# Revit family: XLWH_SUPPLY
name_source: partatom
category: Mechanical Equipment
units: mm (PartAtom-declared; Revit-internal decimal feet)

## family parameters
Always vertical = Yes
Cut with Voids When Loaded = No
Part Type = Normal
Room Calculation Point = No
Round Connector Dimension = Use Diameter
Shared = No
Work Plane-Based = No

## types (8) — shared parameters
0 = 0' - 0"
1" = 0' - 1"
1.5 = 0' - 1 1/2"
1/2 = 0' - 0 1/2"
2" = 0' - 2"
2' = 2' - 0"
3" = 0' - 3"
4" = 0' - 4"
4'6" = 4' - 6"
9" = 0' - 9"
Manufacturer = Loren Cook Company
Model = XLWH_Supply
ONE EIGTH = 0' - 0 1/8"
Type Comments = Heavy Duty Low-Pressure Wall Supply Fan Steel Propeller Belt Drive
URL = www.lorencook.com

## per-type parameters (varying)
- 24_XLWH_SUPPLY: (A/2)-1"=1' - 2 27/32"; (A/2)-C-.5"=0' - 7 27/32"; (D_SUP/2)-(C/2)-.125"=0' - 11 1/2"; (SIZE/2)-.25"=1' - 2 11/16"; -((A/2)-C-.5")=-0' - 7 27/32"; -((SIZE/2)-.25")=-1' - 2 11/16"; -B=-1' - 7 1/16"; -B+1"=-1' - 5 1/16"; -C/2=-0' - 3 3/8"; -D=-0' - 3"; A=2' - 6 3/16"; A/2=1' - 3 3/32"; A/3.5=0' - 8 5/8"; A/7=0' - 4 5/16"; B=1' - 7 1/16"; B/2=0' - 9 17/32"; B/4=0' - 4 25/32"; C=0' - 6 3/4"; C/2=0' - 3 3/8"; D=2' - 6"; D/2=1' - 3"; E=0' - 3"; E/2=0' - 1 1/2"; MOTOR=0' - 3"; SIZE=2' - 5 7/8"; SIZE/2=1' - 2 15/16"
- 30_XLWH_SUPPLY: (A/2)-1"=1' - 5 27/32"; (A/2)-C-.5"=0' - 10 27/32"; (D_SUP/2)-(C/2)-.125"=1' - 2 1/2"; (SIZE/2)-.25"=1' - 5 11/16"; -((A/2)-C-.5")=-0' - 10 27/32"; -((SIZE/2)-.25")=-1' - 5 11/16"; -B=-1' - 7 1/16"; -B+1"=-1' - 5 1/16"; -C/2=-0' - 3 3/8"; -D=-0' - 3"; A=3' - 0 3/16"; A/2=1' - 6 3/32"; A/3.5=0' - 10 11/32"; A/7=0' - 5 5/32"; B=1' - 7 1/16"; B/2=0' - 9 17/32"; B/4=0' - 4 25/32"; C=0' - 6 3/4"; C/2=0' - 3 3/8"; D=3' - 0"; D/2=1' - 6"; E=0' - 3"; E/2=0' - 1 1/2"; MOTOR=0' - 3 19/32"; SIZE=2' - 11 7/8"; SIZE/2=1' - 5 15/16"
- 36_XLWH_SUPPLY: (A/2)-1"=1' - 8 27/32"; (A/2)-C-.5"=1' - 1 7/32"; (D_SUP/2)-(C/2)-.125"=1' - 5 3/16"; (SIZE/2)-.25"=1' - 8 11/16"; -((A/2)-C-.5")=-1' - 1 7/32"; -((SIZE/2)-.25")=-1' - 8 11/16"; -B=-1' - 7 1/16"; -B+1"=-1' - 5 1/16"; -C/2=-0' - 3 11/16"; -D=-0' - 3"; A=3' - 6 3/16"; A/2=1' - 9 3/32"; A/3.5=1' - 0 1/16"; A/7=0' - 6 1/32"; B=1' - 7 1/16"; B/2=0' - 9 17/32"; B/4=0' - 4 25/32"; C=0' - 7 3/8"; C/2=0' - 3 11/16"; D=3' - 6"; D/2=1' - 9"; E=0' - 3"; E/2=0' - 1 1/2"; MOTOR=0' - 4 3/16"; SIZE=3' - 5 7/8"; SIZE/2=1' - 8 15/16"
- 42_XLWH_SUPPLY: (A/2)-1"=1' - 11 27/32"; (A/2)-C-.5"=1' - 4 1/32"; (D_SUP/2)-(C/2)-.125"=1' - 8 3/32"; (SIZE/2)-.25"=1' - 11 11/16"; -((A/2)-C-.5")=-1' - 4 1/32"; -((SIZE/2)-.25")=-1' - 11 11/16"; -B=-1' - 8 11/16"; -B+1"=-1' - 6 11/16"; -C/2=-0' - 3 25/32"; -D=-0' - 3"; A=4' - 0 3/16"; A/2=2' - 0 3/32"; A/3.5=1' - 1 25/32"; A/7=0' - 6 7/8"; B=1' - 8 11/16"; B/2=0' - 10 11/32"; B/4=0' - 5 3/16"; C=0' - 7 9/16"; C/2=0' - 3 25/32"; D=4' - 0"; D/2=2' - 0"; E=0' - 3"; E/2=0' - 1 1/2"; MOTOR=0' - 4 13/16"; SIZE=3' - 11 7/8"; SIZE/2=1' - 11 15/16"
- 48_XLWH_SUPPLY: (A/2)-1"=2' - 2 27/32"; (A/2)-C-.5"=1' - 6 23/32"; (D_SUP/2)-(C/2)-.125"=1' - 10 15/16"; (SIZE/2)-.25"=2' - 2 11/16"; -((A/2)-C-.5")=-1' - 6 23/32"; -((SIZE/2)-.25")=-2' - 2 11/16"; -B=-2' - 2 5/16"; -B+1"=-2' - 0 5/16"; -C/2=-0' - 3 15/16"; -D=-0' - 3"; A=4' - 6 3/16"; A/2=2' - 3 3/32"; A/3.5=1' - 3 15/32"; A/7=0' - 7 3/4"; B=2' - 2 5/16"; B/2=1' - 1 5/32"; B/4=0' - 6 19/32"; C=0' - 7 7/8"; C/2=0' - 3 15/16"; D=4' - 6"; D/2=2' - 3"; E=0' - 3"; E/2=0' - 1 1/2"; MOTOR=0' - 5 13/32"; SIZE=4' - 5 7/8"; SIZE/2=2' - 2 15/16"
- 54_XLWH_SUPPLY: (A/2)-1"=2' - 5 27/32"; (A/2)-C-.5"=1' - 9 27/32"; (D_SUP/2)-(C/2)-.125"=2' - 2"; (SIZE/2)-.25"=2' - 5 11/16"; -((A/2)-C-.5")=-1' - 9 27/32"; -((SIZE/2)-.25")=-2' - 5 11/16"; -B=-2' - 2 5/16"; -B+1"=-2' - 0 5/16"; -C/2=-0' - 3 7/8"; -D=-0' - 3"; A=5' - 0 3/16"; A/2=2' - 6 3/32"; A/3.5=1' - 5 3/16"; A/7=0' - 8 19/32"; B=2' - 2 5/16"; B/2=1' - 1 5/32"; B/4=0' - 6 19/32"; C=0' - 7 3/4"; C/2=0' - 3 7/8"; D=5' - 0"; D/2=2' - 6"; E=0' - 3"; E/2=0' - 1 1/2"; MOTOR=0' - 6"; SIZE=4' - 11 7/8"; SIZE/2=2' - 5 15/16"
- 60_XLWH_SUPPLY: (A/2)-1"=2' - 8 27/32"; (A/2)-C-.5"=2' - 0 23/32"; (D_SUP/2)-(C/2)-.125"=2' - 4 15/16"; (SIZE/2)-.25"=2' - 8 11/16"; -((A/2)-C-.5")=-2' - 0 23/32"; -((SIZE/2)-.25")=-2' - 8 11/16"; -B=-2' - 2 5/16"; -B+1"=-2' - 0 5/16"; -C/2=-0' - 3 15/16"; -D=-0' - 3"; A=5' - 6 3/16"; A/2=2' - 9 3/32"; A/3.5=1' - 6 29/32"; A/7=0' - 9 15/32"; B=2' - 2 5/16"; B/2=1' - 1 5/32"; B/4=0' - 6 19/32"; C=0' - 7 7/8"; C/2=0' - 3 15/16"; D=5' - 6"; D/2=2' - 9"; E=0' - 3"; E/2=0' - 1 1/2"; MOTOR=0' - 6 19/32"; SIZE=5' - 5 7/8"; SIZE/2=2' - 8 15/16"
- 20_XLWH_Supply: (A/2)-1"=0' - 11 27/32"; (A/2)-C-.5"=0' - 6 11/32"; (D_SUP/2)-(C/2)-.125"=0' - 9 1/4"; (SIZE/2)-.25"=0' - 11 11/16"; -((A/2)-C-.5")=-0' - 6 11/32"; -((SIZE/2)-.25")=-0' - 11 11/16"; -B=-1' - 7 1/16"; -B+1"=-1' - 5 1/16"; -C/2=-0' - 2 5/8"; -D=-0' - 2"; A=2' - 0 3/16"; A/2=1' - 0 3/32"; A/3.5=0' - 6 29/32"; A/7=0' - 3 15/32"; B=1' - 7 1/16"; B/2=0' - 9 17/32"; B/4=0' - 4 25/32"; C=0' - 5 1/4"; C/2=0' - 2 5/8"; D=2' - 0"; D/2=1' - 0"; E=0' - 2"; E/2=0' - 1"; MOTOR=0' - 2 13/32"; SIZE=1' - 11 7/8"; SIZE/2=0' - 11 15/16"

## geometry (parser evidence)
native form markers: Sweep x2
no freeform markers — native parametric forms only
